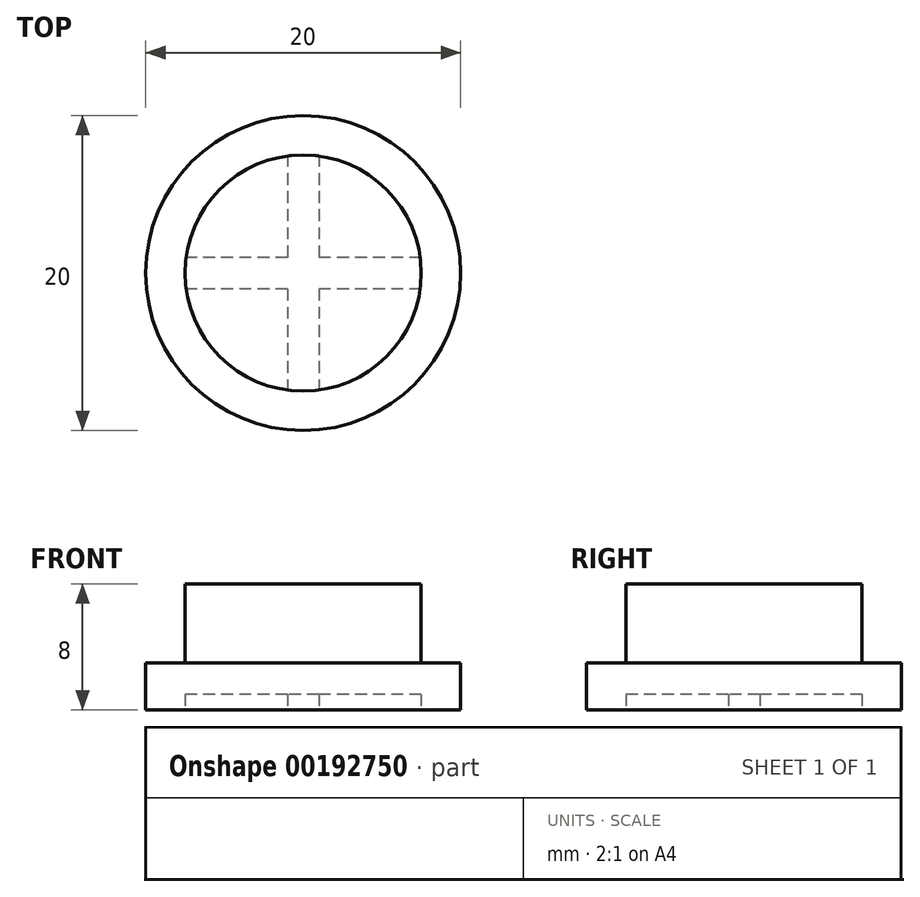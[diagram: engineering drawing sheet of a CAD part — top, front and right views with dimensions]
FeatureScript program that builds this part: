
annotation { "Feature Type Name" : "Feature", "Feature Type Description" : "" }
export const myFeature = defineFeature(function(context is Context, id is Id, definition is map)
    precondition{}
    {
        {
            var Q0;
            Q0=qCreatedBy(makeId("Top.planeOp"),FACE);
            var sketch = newSketch(context, id + "F0", { "sketchPlane" : qUnion([Q0])});
            skCircle(sketch, "E0", {"center": v(0, 0) * mm, "radius": 10 * mm});
            skSolve(sketch);
        }
        {
            var Q0;
            Q0 = qSketchRegion(id + "F0", true);
            extrude(context, id + "F1", {"entities" : qUnion([Q0]), "depth" : 3 * mm});
        }
        {
            var Q0;
            Q0=makeQuery(id+"F1.opExtrude","CAP_FACE",FACE,{"disambiguationData":[OSD([sQuery(id+"F0.wireOp",EDGE,"E0")])],"isStart":false});
            var sketch = newSketch(context, id + "F2", { "sketchPlane" : qUnion([Q0])});
            skCircle(sketch, "E1", {"center": v(0, 0) * mm, "radius": 7.5 * mm});
            skSolve(sketch);
        }
        {
            var Q0;
            Q0 = qSketchRegion(id + "F2", true);
            extrude(context, id + "F3", {"entities" : qUnion([Q0]), "operationType" : NewBodyOperationType.ADD, "depth" : 5 * mm});
        }
        {
            var Q0;
            Q0=makeQuery(id+"F1.opExtrude","CAP_FACE",FACE,{"disambiguationData":[OSD([sQuery(id+"F0.wireOp",EDGE,"E0")])],"isStart":true});
            var sketch = newSketch(context, id + "F4", { "sketchPlane" : qUnion([Q0])});
            skLineSegment(sketch, "E2.bottom", {"start": v(7.5, -1) * mm, "end": v(-7.5, -1) * mm});
            skLineSegment(sketch, "E2.top", {"start": v(7.5, 1) * mm, "end": v(-7.5, 1) * mm});
            skLineSegment(sketch, "E2.left", {"start": v(7.5, -1) * mm, "end": v(7.5, 1) * mm});
            skLineSegment(sketch, "E2.right", {"start": v(-7.5, -1) * mm, "end": v(-7.5, 1) * mm});
            skPoint(sketch, "E2.middle", {"position": v(0, 0) * mm});
            skLineSegment(sketch, "E3.bottom", {"start": v(1, -7.5) * mm, "end": v(-1, -7.5) * mm});
            skLineSegment(sketch, "E3.top", {"start": v(1, 7.5) * mm, "end": v(-1, 7.5) * mm});
            skLineSegment(sketch, "E3.left", {"start": v(1, -7.5) * mm, "end": v(1, 7.5) * mm});
            skLineSegment(sketch, "E3.right", {"start": v(-1, -7.5) * mm, "end": v(-1, 7.5) * mm});
            skSolve(sketch);
        }
        {
            var Q0;
            Q0 = qSketchRegion(id + "F4", true);
            extrude(context, id + "F5", {"entities" : qUnion([Q0]), "operationType" : NewBodyOperationType.REMOVE, "oppositeDirection" : true, "depth" : 1 * mm});
        }
    });
